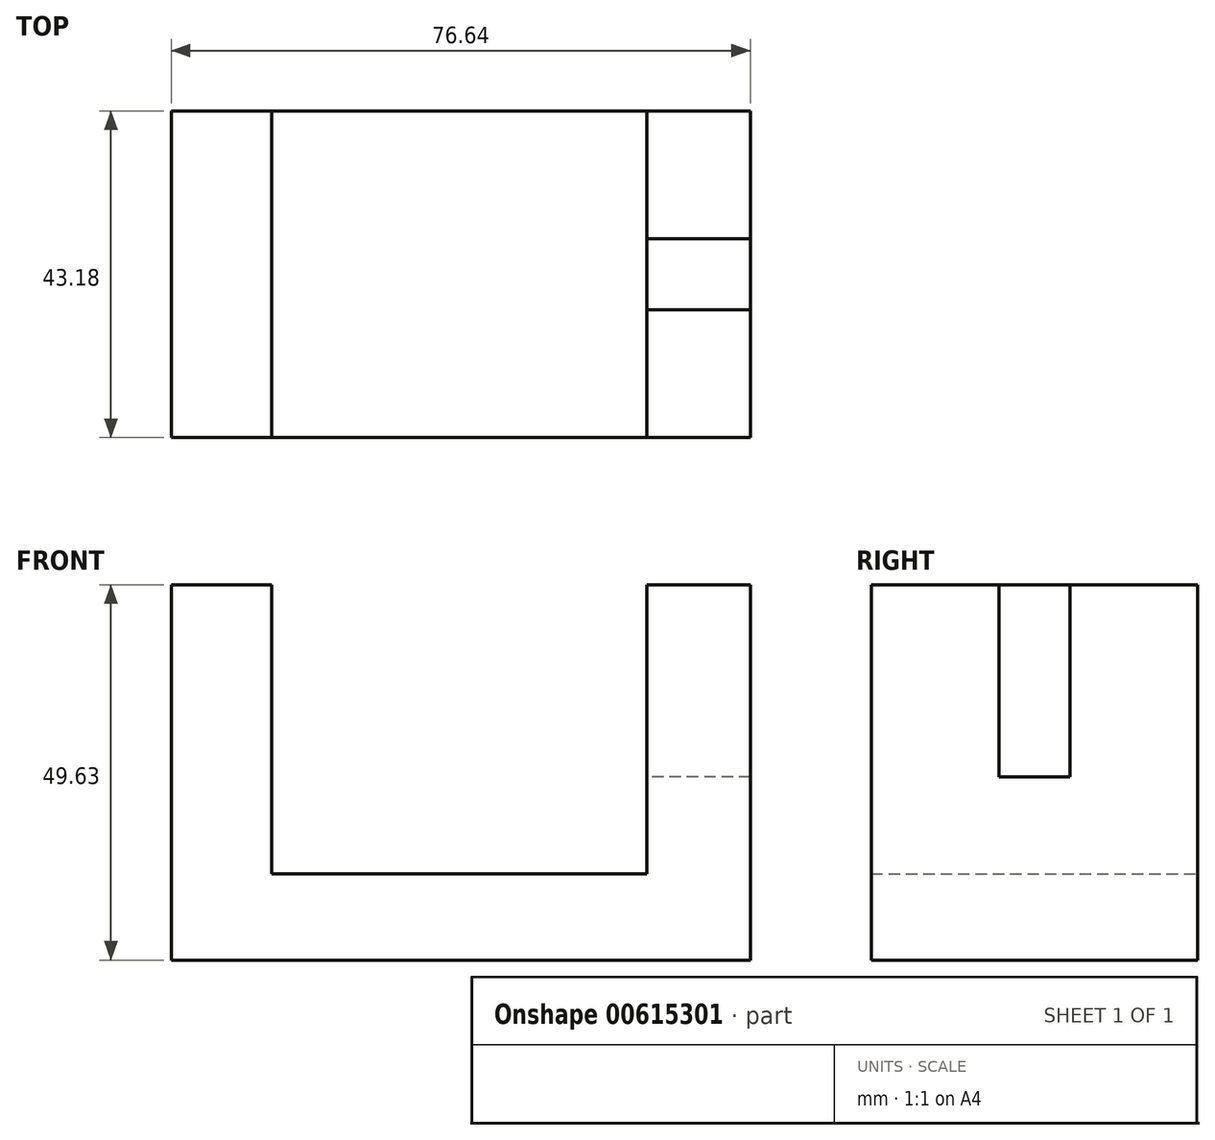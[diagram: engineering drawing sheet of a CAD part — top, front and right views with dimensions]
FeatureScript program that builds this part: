
annotation { "Feature Type Name" : "Feature", "Feature Type Description" : "" }
export const myFeature = defineFeature(function(context is Context, id is Id, definition is map)
    precondition{}
    {
        {
            var Q0;
            Q0=qCreatedBy(makeId("Front.planeOp"),FACE);
            var sketch = newSketch(context, id + "F0", { "sketchPlane" : qUnion([Q0])});
            skLineSegment(sketch, "E0.bottom", {"start": v(0, 0) * mm, "end": v(76.64, 0) * mm});
            skLineSegment(sketch, "E0.left", {"start": v(0, 0) * mm, "end": v(0, 49.63) * mm});
            skLineSegment(sketch, "E0.right", {"start": v(76.64, 0) * mm, "end": v(76.64, 49.63) * mm});
            skLineSegment(sketch, "E1.top", {"start": v(38.32, 11.39) * mm, "end": v(13.28, 11.39) * mm});
            skLineSegment(sketch, "E1.right", {"start": v(13.28, 49.63) * mm, "end": v(13.28, 11.39) * mm});
            skLineSegment(sketch, "E2.top", {"start": v(38.32, 11.39) * mm, "end": v(62.92, 11.39) * mm});
            skLineSegment(sketch, "E2.right", {"start": v(62.92, 49.63) * mm, "end": v(62.92, 11.39) * mm});
            skPoint(sketch, "E1.bottom.start.orphan", {"position": v(38.32, 49.63) * mm});
            skLineSegment(sketch, "E3.trimOffspring", {"start": v(62.92, 49.63) * mm, "end": v(76.64, 49.63) * mm});
            skLineSegment(sketch, "E4", {"start": v(0, 49.63) * mm, "end": v(13.28, 49.63) * mm});
            skSolve(sketch);
        }
        {
            var Q0;
            Q0=makeQuery(id+"F0.imprint","IMPRINT",FACE,{"disambiguationData":[TD([[makeQuery(id+"F0.imprint","IMPRINT",EDGE,{"derivedFrom":sQuery(id+"F0.wireOp",EDGE,"E0.bottom")}),1.0]])]});
            extrude(context, id + "F1", {"entities" : qUnion([Q0]), "depth" : 43.18 * mm, "offsetDistance" : 25.4 * mm});
        }
        {
            var Q0;
            Q0=makeQuery(id+"F1.opExtrude","SWEPT_FACE",FACE,{"disambiguationData":[OSD([sQuery(id+"F0.wireOp",EDGE,"E3.trimOffspring")])]});
            var sketch = newSketch(context, id + "F2", { "sketchPlane" : qUnion([Q0])});
            skLineSegment(sketch, "E5.bottom", {"start": v(76.64, -26.3) * mm, "end": v(62.92, -26.3) * mm});
            skLineSegment(sketch, "E5.top", {"start": v(76.64, -16.89) * mm, "end": v(62.92, -16.89) * mm});
            skLineSegment(sketch, "E5.left", {"start": v(76.64, -26.3) * mm, "end": v(76.64, -16.89) * mm});
            skPoint(sketch, "E5.middle", {"position": v(62.92, -21.59) * mm});
            skLineSegment(sketch, "E6", {"start": v(62.92, -26.3) * mm, "end": v(62.92, -16.89) * mm});
            skPoint(sketch, "E7.orphan", {"position": v(49.2, -26.3) * mm});
            skPoint(sketch, "E8.orphan", {"position": v(49.2, -16.89) * mm});
            skSolve(sketch);
        }
        {
            var Q0;
            Q0=makeQuery(id+"F2.imprint","IMPRINT",FACE,{"disambiguationData":[TD([[makeQuery(id+"F2.imprint","IMPRINT",EDGE,{"derivedFrom":sQuery(id+"F2.wireOp",EDGE,"E5.bottom")}),-1.0]])]});
            extrude(context, id + "F3", {"entities" : qUnion([Q0]), "operationType" : NewBodyOperationType.REMOVE, "oppositeDirection" : true, "depth" : 25.4 * mm, "offsetDistance" : 25.4 * mm});
        }
    });
